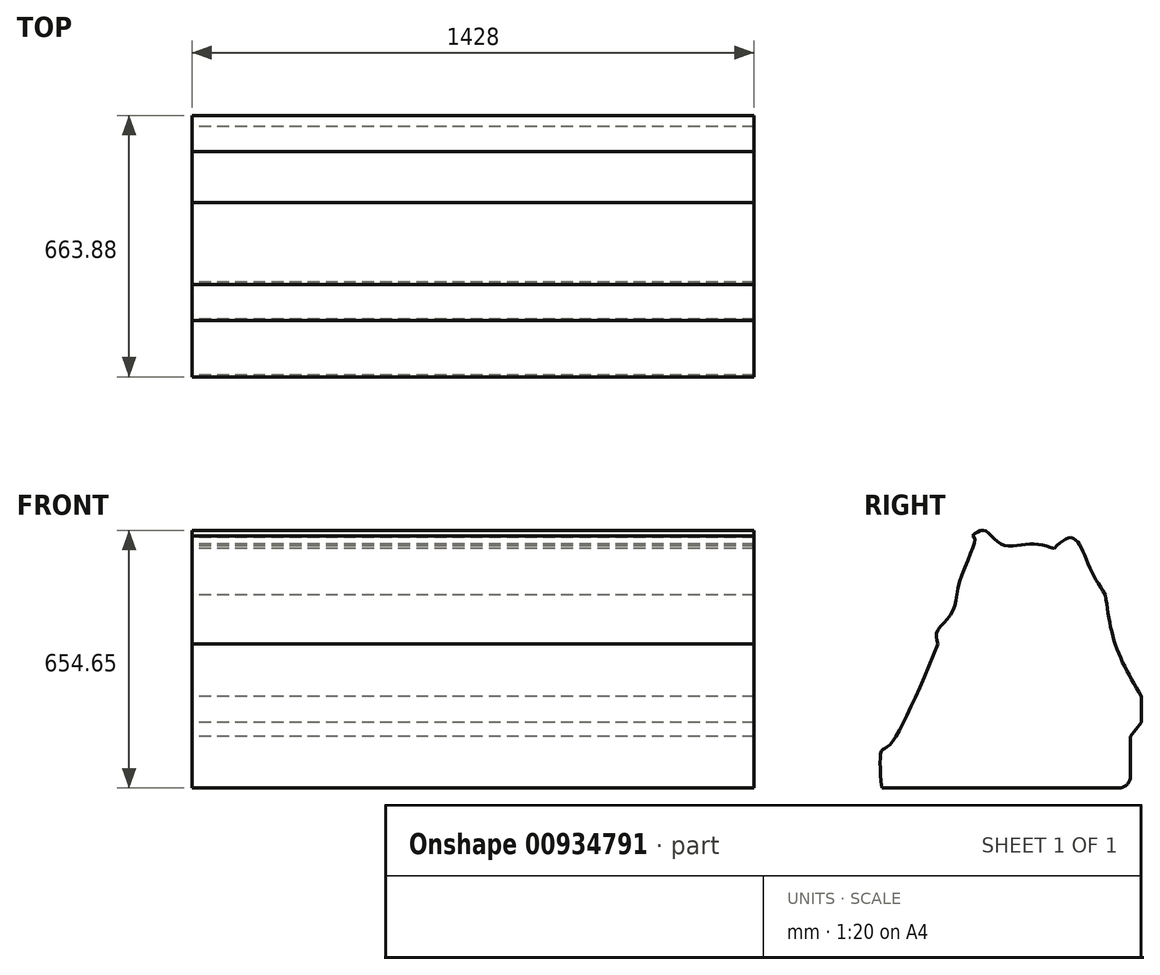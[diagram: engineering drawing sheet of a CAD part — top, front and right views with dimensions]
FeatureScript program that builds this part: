
annotation { "Feature Type Name" : "Feature", "Feature Type Description" : "" }
export const myFeature = defineFeature(function(context is Context, id is Id, definition is map)
    precondition{}
    {
        {
            var Q0;
            Q0=qCreatedBy(makeId("Right.planeOp"),FACE);
            var sketch = newSketch(context, id + "F0", { "sketchPlane" : qUnion([Q0])});
            skLineSegment(sketch, "E0", {"start": v(0, 0) * mm, "end": v(602, 0) * mm});
            skLineSegment(sketch, "E1", {"start": v(632, 30) * mm, "end": v(632, 131.64) * mm});
            skLineSegment(sketch, "E2", {"start": v(632, 131.64) * mm, "end": v(659.57, 166.68) * mm});
            skLineSegment(sketch, "E3", {"start": v(659.57, 166.68) * mm, "end": v(659.57, 232.74) * mm});
            skFitSpline(sketch, "E4", {"points": [v(659.57, 232.74) * mm, v(594.75, 360.85) * mm, v(568.4, 490.78) * mm], "startDerivative": vector(-145.81, 247.67) * mm, "endDerivative": vector(-35.8, 268.56) * mm});
            skFitSpline(sketch, "E5", {"points": [v(568.4, 490.78) * mm, v(528.56, 558.94) * mm, v(500.12, 622.14) * mm, v(476.95, 635.83) * mm, v(437.97, 608.45) * mm], "startDerivative": vector(-142.23, 216.1) * mm, "endDerivative": vector(-173.4, -165.14) * mm});
            skFitSpline(sketch, "E6", {"points": [v(437.97, 608.45) * mm, v(372.67, 620.03) * mm, v(306.31, 617.93) * mm, v(260.97, 653.94) * mm, v(230, 640.8) * mm], "startDerivative": vector(-232.72, 71.12) * mm, "endDerivative": vector(-158.26, -125.47) * mm});
            skFitSpline(sketch, "E7", {"points": [v(230, 640.8) * mm, v(236.57, 630.48) * mm, v(199.03, 528.2) * mm, v(177.45, 443.74) * mm, v(140.85, 397.76) * mm, v(142.73, 365.86) * mm], "startDerivative": vector(100.4, -72.96) * mm, "endDerivative": vector(61.54, -207.97) * mm});
            skFitSpline(sketch, "E8", {"points": [v(142.73, 365.86) * mm, v(17, 106.63) * mm, v(0, 94.54) * mm, v(0, 0) * mm], "startDerivative": vector(-270.3, -649.84) * mm, "endDerivative": vector(36.05, -395.03) * mm});
            skPoint(sketch, "E9.visualSharp", {"position": v(632, 0) * mm});
            skArc(sketch, "E9.filletArc", {"start": v(602, 0) * mm, "mid": v(623.21, 8.79) * mm, "end": v(632, 30) * mm});
            skSolve(sketch);
        }
        {
            var Q0;
            Q0=makeQuery(id+"F0.imprint","IMPRINT",FACE,{"disambiguationData":[TD([[makeQuery(id+"F0.imprint","IMPRINT",EDGE,{"derivedFrom":sQuery(id+"F0.wireOp",EDGE,"E0")}),1.0]])]});
            extrude(context, id + "F1", {"entities" : qUnion([Q0]), "depth" : 1428 * mm, "offsetDistance" : 25 * mm});
        }
    });
